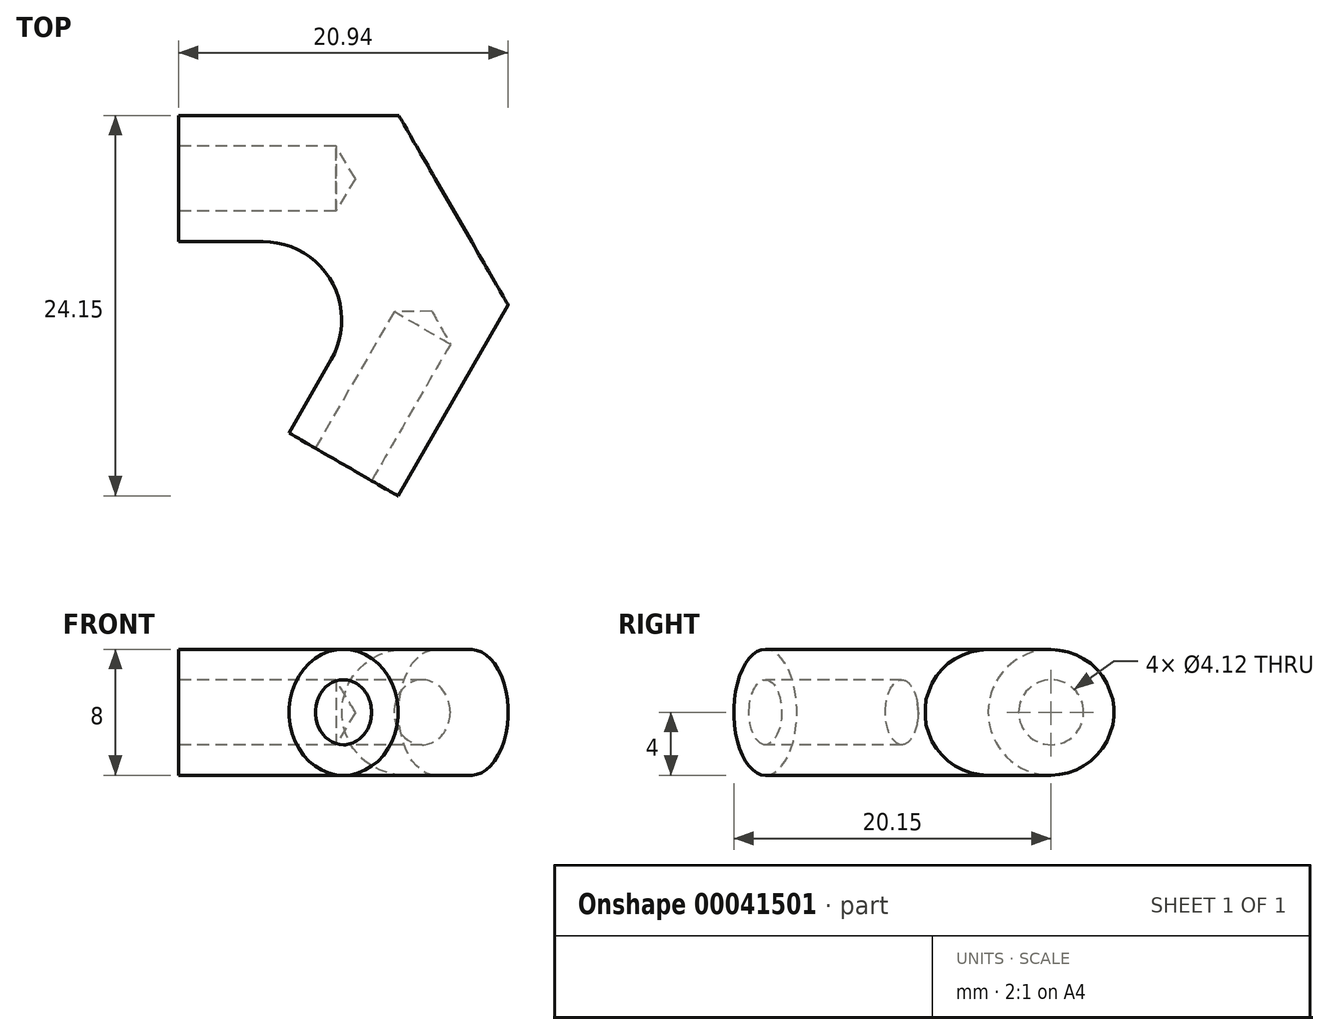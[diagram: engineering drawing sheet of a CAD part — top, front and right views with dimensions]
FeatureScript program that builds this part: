
annotation { "Feature Type Name" : "Feature", "Feature Type Description" : "" }
export const myFeature = defineFeature(function(context is Context, id is Id, definition is map)
    precondition{}
    {
        {
            var Q0;
            Q0=qCreatedBy(makeId("Top.planeOp"),FACE);
            var sketch = newSketch(context, id + "F0", { "sketchPlane" : qUnion([Q0])});
            skLineSegment(sketch, "E0", {"start": v(0, 0) * mm, "end": v(25.98, -15) * mm, "construction": true});
            skLineSegment(sketch, "E1", {"start": v(36.23, 2.75) * mm, "end": v(15.73, -32.75) * mm, "construction": true});
            skLineSegment(sketch, "E2", {"start": v(15.73, -32.75) * mm, "end": v(10.48, -41.85) * mm, "construction": true});
            skLineSegment(sketch, "E3", {"start": v(36.23, 2.75) * mm, "end": v(41.48, 11.85) * mm, "construction": true});
            skLineSegment(sketch, "E4", {"start": v(-20.5, 30) * mm, "end": v(20.5, 30) * mm, "construction": true});
            skLineSegment(sketch, "E5", {"start": v(20.5, 30) * mm, "end": v(31, 30) * mm, "construction": true});
            skLineSegment(sketch, "E6", {"start": v(-20.5, 30) * mm, "end": v(-31, 30) * mm, "construction": true});
            skLineSegment(sketch, "E7", {"start": v(0, 0) * mm, "end": v(0, 30) * mm, "construction": true});
            skLineSegment(sketch, "E8", {"start": v(-15.73, -32.75) * mm, "end": v(-36.23, 2.75) * mm, "construction": true});
            skLineSegment(sketch, "E9", {"start": v(-36.23, 2.75) * mm, "end": v(-41.48, 11.85) * mm, "construction": true});
            skLineSegment(sketch, "E10", {"start": v(-15.73, -32.75) * mm, "end": v(-10.48, -41.85) * mm, "construction": true});
            skLineSegment(sketch, "E11", {"start": v(0, 0) * mm, "end": v(-25.98, -15) * mm, "construction": true});
            skLineSegment(sketch, "E12", {"start": v(41.48, 11.85) * mm, "end": v(51.96, 30) * mm, "construction": true});
            skLineSegment(sketch, "E13", {"start": v(51.96, 30) * mm, "end": v(31, 30) * mm, "construction": true});
            skLineSegment(sketch, "E14", {"start": v(-31, 30) * mm, "end": v(-51.96, 30) * mm, "construction": true});
            skLineSegment(sketch, "E15", {"start": v(-51.96, 30) * mm, "end": v(-41.48, 11.85) * mm, "construction": true});
            skLineSegment(sketch, "E16", {"start": v(-10.48, -41.85) * mm, "end": v(0, -60) * mm, "construction": true});
            skLineSegment(sketch, "E17", {"start": v(0, -60) * mm, "end": v(10.48, -41.85) * mm, "construction": true});
            skLineSegment(sketch, "E18", {"start": v(31, 34) * mm, "end": v(31, 26) * mm});
            skLineSegment(sketch, "E19", {"start": v(38.02, 13.85) * mm, "end": v(44.94, 9.85) * mm});
            skLineSegment(sketch, "E20", {"start": v(38.02, 13.85) * mm, "end": v(40.7, 18.5) * mm});
            skLineSegment(sketch, "E21", {"start": v(36.37, 26) * mm, "end": v(31, 26) * mm});
            skLineSegment(sketch, "E22", {"start": v(44.94, 9.85) * mm, "end": v(51.94, 21.97) * mm});
            skLineSegment(sketch, "E23", {"start": v(45, 34) * mm, "end": v(31, 34) * mm});
            skPoint(sketch, "E24.visualSharp", {"position": v(45.03, 26) * mm});
            skArc(sketch, "E24.filletArc", {"start": v(40.7, 18.5) * mm, "mid": v(40.7, 23.5) * mm, "end": v(36.37, 26) * mm});
            skLineSegment(sketch, "E25", {"start": v(45, 34) * mm, "end": v(51.94, 21.97) * mm});
            skSolve(sketch);
        }
        {
            var Q0;
            Q0 = qSketchRegion(id + "F0", true);
            extrude(context, id + "F1", {"entities" : qUnion([Q0]), "depth" : 8 * mm});
        }
        {
            var Q0;
            Q0=makeQuery(id+"F1.opExtrude","CAP_EDGE",EDGE,{"disambiguationData":[OSD([sQuery(id+"F0.wireOp",EDGE,"E22")])],"isStart":false});
            var Q1;
            Q1=makeQuery(id+"F1.opExtrude","CAP_EDGE",EDGE,{"disambiguationData":[OSD([sQuery(id+"F0.wireOp",EDGE,"E22")])],"isStart":true});
            var Q2;
            Q2=makeQuery(id+"F1.opExtrude","CAP_EDGE",EDGE,{"disambiguationData":[OSD([sQuery(id+"F0.wireOp",EDGE,"E23")])],"isStart":false});
            var Q3;
            Q3=makeQuery(id+"F1.opExtrude","CAP_EDGE",EDGE,{"disambiguationData":[OSD([sQuery(id+"F0.wireOp",EDGE,"E23")])],"isStart":true});
            fillet(context, id + "F2", {"entities" : qUnion([Q0, Q1, Q2, Q3]), "radius" : 4 * mm, "allowEdgeOverflow" : false});
        }
        {
            var Q0;
            Q0=makeQuery(id+"F1.opExtrude","CAP_EDGE",EDGE,{"disambiguationData":[OSD([sQuery(id+"F0.wireOp",EDGE,"E21")])],"isStart":false});
            var Q1;
            Q1=makeQuery(id+"F1.opExtrude","CAP_EDGE",EDGE,{"disambiguationData":[OSD([sQuery(id+"F0.wireOp",EDGE,"E21")])],"isStart":true});
            var Q2;
            Q2=makeQuery(id+"F1.opExtrude","CAP_EDGE",EDGE,{"disambiguationData":[OSD([sQuery(id+"F0.wireOp",EDGE,"E20")])],"isStart":false});
            var Q3;
            Q3=makeQuery(id+"F1.opExtrude","CAP_EDGE",EDGE,{"disambiguationData":[OSD([sQuery(id+"F0.wireOp",EDGE,"E20")])],"isStart":true});
            fillet(context, id + "F3", {"entities" : qUnion([Q0, Q1, Q2, Q3]), "radius" : 4 * mm, "tangentPropagation" : true, "allowEdgeOverflow" : false});
        }
        {
            var Q0;
            Q0=makeQuery(id+"F1.opExtrude","SWEPT_FACE",FACE,{"disambiguationData":[OSD([sQuery(id+"F0.wireOp",EDGE,"E18")])]});
            var sketch = newSketch(context, id + "F4", { "sketchPlane" : qUnion([Q0])});
            skPoint(sketch, "E26", {"position": v(-30, 4) * mm});
            skSolve(sketch);
        }
        {
            var Q0;
            Q0=makeQuery(id+"F1.opExtrude","SWEPT_FACE",FACE,{"disambiguationData":[OSD([sQuery(id+"F0.wireOp",EDGE,"E19")])]});
            var sketch = newSketch(context, id + "F5", { "sketchPlane" : qUnion([Q0])});
            skPoint(sketch, "E27", {"position": v(30, 4) * mm});
            skSolve(sketch);
        }
        {
            var Q0;
            Q0=sQuery(id+"F4.wireOp",VERTEX,"E26");
            var Q1;
            Q1=sQuery(id+"F5.wireOp",VERTEX,"E27");
            var Q2;
            Q2=makeQuery(id+"F1.opExtrude","SWEPT_BODY",BODY,{"disambiguationData":[OSD([sQuery(id+"F0.wireOp",EDGE,"E18"),sQuery(id+"F0.wireOp",EDGE,"E19"),sQuery(id+"F0.wireOp",EDGE,"E20"),sQuery(id+"F0.wireOp",EDGE,"E21"),sQuery(id+"F0.wireOp",EDGE,"E22"),sQuery(id+"F0.wireOp",EDGE,"E23"),sQuery(id+"F0.wireOp",EDGE,"E24.filletArc"),sQuery(id+"F0.wireOp",EDGE,"E25")])]});
            hole(context, id + "F6", {"style" : HoleStyle.SIMPLE, "holeDiameter" : 4.12 * mm, "endStyle" : HoleEndStyle.BLIND, "holeDepth" : 10 * mm, "locations" : qUnion([Q0, Q1]), "scope" : qUnion([Q2])});
        }
    });
